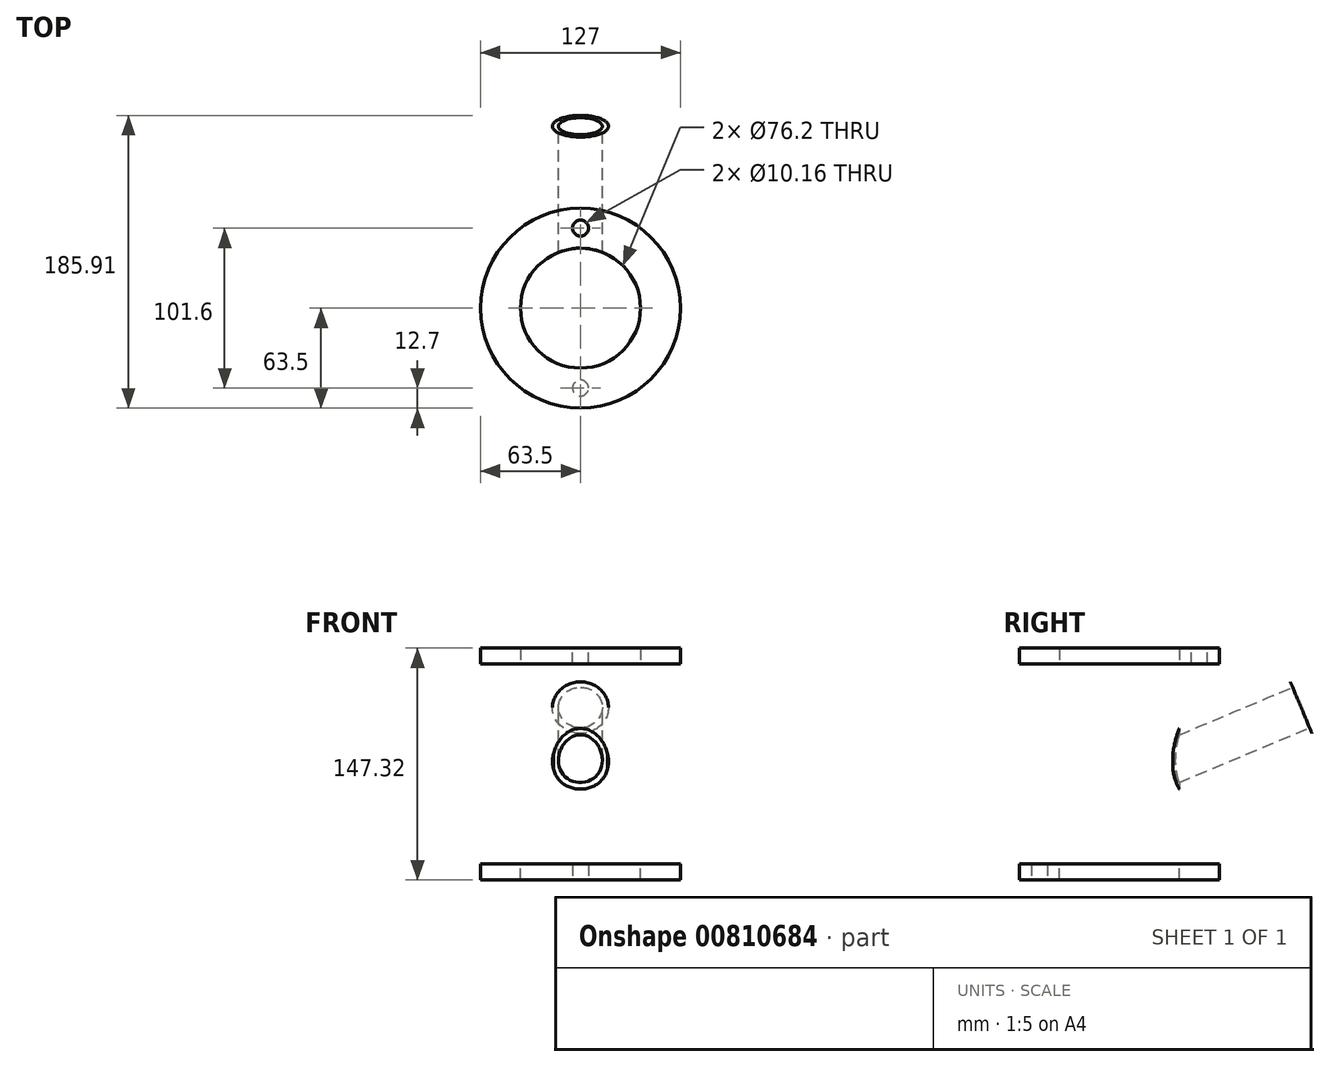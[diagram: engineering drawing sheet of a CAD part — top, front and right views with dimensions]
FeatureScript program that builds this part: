
annotation { "Feature Type Name" : "Feature", "Feature Type Description" : "" }
export const myFeature = defineFeature(function(context is Context, id is Id, definition is map)
    precondition{}
    {
        {
            var Q0;
            Q0=qCreatedBy(makeId("Top.planeOp"),FACE);
            var sketch = newSketch(context, id + "F0", { "sketchPlane" : qUnion([Q0])});
            skCircle(sketch, "E0", {"center": v(0, 0) * mm, "radius": 63.5 * mm});
            skCircle(sketch, "E1", {"center": v(0, 0) * mm, "radius": 38.1 * mm});
            skSolve(sketch);
        }
        {
            var Q0;
            Q0 = qSketchRegion(id + "F0", true);
            extrude(context, id + "F1", {"entities" : qUnion([Q0]), "depth" : 10.16 * mm, "offsetDistance" : 25.4 * mm});
        }
        {
            var Q0;
            Q0=makeQuery(id+"F1.opExtrude","CAP_FACE",FACE,{"disambiguationData":[OSD([sQuery(id+"F0.wireOp",EDGE,"E0"),sQuery(id+"F0.wireOp",EDGE,"E1")])],"isStart":false});
            var sketch = newSketch(context, id + "F2", { "sketchPlane" : qUnion([Q0])});
            skCircle(sketch, "E2", {"center": v(0, 50.8) * mm, "radius": 5.08 * mm});
            skCircle(sketch, "E3", {"center": v(0, 0) * mm, "radius": 50.8 * mm, "construction": true});
            skCircle(sketch, "E4.MirrorC", {"center": v(0, -50.8) * mm, "radius": 5.08 * mm});
            skSolve(sketch);
        }
        {
            var Q0;
            Q0=makeQuery(id+"F2.imprint","IMPRINT",FACE,{"disambiguationData":[TD([[makeQuery(id+"F2.imprint","IMPRINT",EDGE,{"derivedFrom":sQuery(id+"F2.wireOp",EDGE,"E2")}),1.0]])]});
            extrude(context, id + "F3", {"entities" : qUnion([Q0]), "operationType" : NewBodyOperationType.REMOVE, "oppositeDirection" : true, "depth" : 10.16 * mm, "offsetDistance" : 25.4 * mm});
        }
        {
            var Q0;
            Q0=qCreatedBy(makeId("Top.planeOp"),FACE);
            var sketch = newSketch(context, id + "F4", { "sketchPlane" : qUnion([Q0])});
            skCircle(sketch, "E5", {"center": v(0, 0) * mm, "radius": 38.1 * mm});
            skSolve(sketch);
        }
        {
            var Q0;
            Q0 = qSketchRegion(id + "F4", true);
            var Q1;
            Q1=sQuery(id+"F4.wireOp",EDGE,"E5");
            extrude(context, id + "F5", {"entities" : qUnion([Q0]), "bodyType" : ToolBodyType.SURFACE, "operationType" : NewBodyOperationType.INTERSECT, "surfaceEntities" : qUnion([Q1]), "oppositeDirection" : true, "depth" : 127 * mm, "offsetDistance" : 25.4 * mm});
        }
        {
            var Q0;
            Q0=qCreatedBy(makeId("Top.planeOp"),FACE);
            cPlane(context, id + "F6", {"entities" : qUnion([Q0]), "cplaneType" : CPlaneType.OFFSET, "offset" : 127 * mm, "oppositeDirection" : true, "width" : 152.4 * mm, "height" : 152.4 * mm});
        }
        {
            var Q0;
            Q0=qCreatedBy(id+"F6.planeOp",FACE);
            var sketch = newSketch(context, id + "F7", { "sketchPlane" : qUnion([Q0])});
            skCircle(sketch, "E6", {"center": v(0, 0) * mm, "radius": 38.1 * mm});
            skCircle(sketch, "E7", {"center": v(0, 0) * mm, "radius": 63.5 * mm});
            skSolve(sketch);
        }
        {
            var Q0;
            Q0=makeQuery(id+"F7.imprint","IMPRINT",FACE,{"disambiguationData":[TD([[makeQuery(id+"F7.imprint","IMPRINT",EDGE,{"derivedFrom":sQuery(id+"F7.wireOp",EDGE,"E6")}),-1.0]])]});
            extrude(context, id + "F8", {"entities" : qUnion([Q0]), "oppositeDirection" : true, "depth" : 10.16 * mm, "offsetDistance" : 25.4 * mm});
        }
        {
            var Q0;
            Q0=makeQuery(id+"F8.opExtrude","CAP_FACE",FACE,{"disambiguationData":[OSD([sQuery(id+"F7.wireOp",EDGE,"E6"),sQuery(id+"F7.wireOp",EDGE,"E7")])],"isStart":false});
            var sketch = newSketch(context, id + "F9", { "sketchPlane" : qUnion([Q0])});
            skCircle(sketch, "E8", {"center": v(0, 50.8) * mm, "radius": 5.08 * mm});
            skSolve(sketch);
        }
        {
            var Q0;
            Q0=makeQuery(id+"F9.imprint","IMPRINT",FACE,{"disambiguationData":[TD([[makeQuery(id+"F9.imprint","IMPRINT",EDGE,{"derivedFrom":sQuery(id+"F9.wireOp",EDGE,"E8")}),1.0]])]});
            extrude(context, id + "F10", {"entities" : qUnion([Q0]), "operationType" : NewBodyOperationType.REMOVE, "oppositeDirection" : true, "depth" : 10.16 * mm, "offsetDistance" : 25.4 * mm});
        }
        {
            var Q0;
            Q0=qCreatedBy(makeId("Right.planeOp"),FACE);
            var sketch = newSketch(context, id + "F11", { "sketchPlane" : qUnion([Q0])});
            skLineSegment(sketch, "E9", {"start": v(34, -81.08) * mm, "end": v(122.4, -43.99) * mm});
            skLineSegment(sketch, "E10", {"start": v(34, -42.52) * mm, "end": v(108.65, -11.2) * mm});
            skLineSegment(sketch, "E11", {"start": v(108.65, -11.2) * mm, "end": v(122.4, -43.99) * mm});
            skLineSegment(sketch, "E12", {"start": v(34, -81.08) * mm, "end": v(34, -42.52) * mm});
            skPoint(sketch, "E13.orphan", {"position": v(0, -95.34) * mm});
            skSolve(sketch);
        }
        {
            var Q0;
            Q0 = qSketchRegion(id + "F11", true);
            extrude(context, id + "F12", {"entities" : qUnion([Q0]), "endBound" : BoundingType.SYMMETRIC, "depth" : 35.56 * mm, "offsetDistance" : 25.4 * mm});
        }
        {
            var Q0;
            Q0=makeQuery(id+"F12.opExtrude","CAP_EDGE",EDGE,{"disambiguationData":[OSD([sQuery(id+"F11.wireOp",EDGE,"E10")])],"isStart":false});
            var Q1;
            Q1=makeQuery(id+"F12.opExtrude","CAP_EDGE",EDGE,{"disambiguationData":[OSD([sQuery(id+"F11.wireOp",EDGE,"E10")])],"isStart":true});
            var Q2;
            Q2=makeQuery(id+"F12.opExtrude","CAP_EDGE",EDGE,{"disambiguationData":[OSD([sQuery(id+"F11.wireOp",EDGE,"E9")])],"isStart":false});
            var Q3;
            Q3=makeQuery(id+"F12.opExtrude","CAP_EDGE",EDGE,{"disambiguationData":[OSD([sQuery(id+"F11.wireOp",EDGE,"E9")])],"isStart":true});
            fillet(context, id + "F13", {"entities" : qUnion([Q0, Q1, Q2, Q3]), "radius" : 17.8 * mm, "tangentPropagation" : true, "allowEdgeOverflow" : false});
        }
        {
            var Q0;
            Q0=makeQuery(id+"F12.opExtrude","SWEPT_FACE",FACE,{"disambiguationData":[OSD([sQuery(id+"F11.wireOp",EDGE,"E11")])]});
            var sketch = newSketch(context, id + "F14", { "sketchPlane" : qUnion([Q0])});
            skCircle(sketch, "E14", {"center": v(0.03, -70.11) * mm, "radius": 17.78 * mm});
            skCircle(sketch, "E15", {"center": v(0.03, -70.11) * mm, "radius": 13.97 * mm});
            skSolve(sketch);
        }
        {
            var Q0;
            Q0=makeQuery(id+"F14.imprint","IMPRINT",FACE,{"disambiguationData":[TD([[makeQuery(id+"F14.imprint","IMPRINT",EDGE,{"derivedFrom":sQuery(id+"F14.wireOp",EDGE,"E15")}),1.0]])]});
            extrude(context, id + "F15", {"entities" : qUnion([Q0]), "operationType" : NewBodyOperationType.REMOVE, "endBound" : BoundingType.THROUGH_ALL, "oppositeDirection" : true, "depth" : 106.68 * mm, "offsetDistance" : 25.4 * mm});
        }
        {
            var Q0;
            Q0=qCreatedBy(id+"F6.planeOp",FACE);
            var sketch = newSketch(context, id + "F16", { "sketchPlane" : qUnion([Q0])});
            skCircle(sketch, "E16", {"center": v(0, 0) * mm, "radius": 38.1 * mm});
            skSolve(sketch);
        }
        {
            var Q0;
            Q0=makeQuery(id+"F16.imprint","IMPRINT",FACE,{"disambiguationData":[TD([[makeQuery(id+"F16.imprint","IMPRINT",EDGE,{"derivedFrom":sQuery(id+"F16.wireOp",EDGE,"E16")}),1.0]])]});
            extrude(context, id + "F17", {"entities" : qUnion([Q0]), "operationType" : NewBodyOperationType.REMOVE, "depth" : 197.87 * mm, "offsetDistance" : 25.4 * mm});
        }
    });
